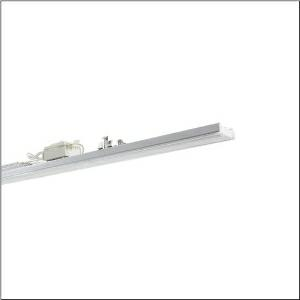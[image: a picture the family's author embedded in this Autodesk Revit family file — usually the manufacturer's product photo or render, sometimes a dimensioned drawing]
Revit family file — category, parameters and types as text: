
# Revit family: licross_11_recessed_mo_51tl12dv4fxg3c
name_source: partatom
category: Lighting Fixtures
units: mm (PartAtom-declared; Revit-internal decimal feet)

## family parameters
Cut with Voids When Loaded = No
Host = Face
Light Source = No
Part Type = Normal
Room Calculation Point = No
Round Connector Dimension = Use Diameter
Shared = No

## types (1)
- --- (1 x LED, 1010 lm, 5.5 W, 4000K)
    Apparent Load = 6 VA
    CIE Flux Codes = 67 92 99 100 100
    Color Rendering = 80
    Color Temperature = 4000K
    Default Elevation = 1800 mm
    Description = Licross 11 Recessed MO, luminaire insert, of sheet steel, coil coated, white, length: 2.250mm, width: 66mm, height: 67mm, LED rated luminous flux: 15.360lm, light colour: 840, SDCM (Standard Deviation of Colour Matching)MacAdam ≤ 2 SDCM (initial), control gear: DALI 2 (for two DALI lines), with plug, 6-pole, with phase selection, for trunking rail, 14-core, mains connection: 220..240V, AC, 50/60Hz, rated input power: 88W, for trunking rail, 14-core, internal wiring halogen-free, for emergency light function, converter,control gear: single battery element, battery: LiFePO4, 9Ah, primary optical cover: cover, of PMMA, light emission: direct distribution, primary light characteristic: symmetric, protection rating (complete): IP40, insulation class (complete): insulation class I (protective earthing), certification: CE, UKCA, protection symbol: D if used in an environment without relevant dust loads with corresponding accessories, impact resistance: IK06, permissible ambient temperature for indoor applications: +5..+35°C, standard: EN 60598-2-22, LABS conformity tested according to VDMA 24364:2018-05, reducing of maximum allowable ambient temperature of 5°C with ceiling mounting, corresponds to IFS (International Featured Standards) requirements for safety and quality in the food industry, The light source and the operating device comply with the requirements of the Ecodesign Regulation (EU) 2019/2020 and are replaceable in accordance with this regulation, packaging unit: 1 piece
    Height = 58 mm
    Lamp = 1 x LED
    Lamp Light Flux = 1010 lm
    Lamp Power = 5.5 W
    Lamp count = 1
    Length = 2250 mm
    Luminous efficacy = 184 lm/W
    Manufacturer = Siteco
    ModVariant = No
    Model = 51TL12DV4FXG3C
    Mounting Place = Ceiling
    Mounting Type = Pendant
    Number of Poles = 1
    OnlyDefault = Yes
    Power Factor = 1
    Product Name = Licross 11 Recessed MO
    Product group = luminaire insert | ceiling pendant
    ProductGroupID = 901
    Protection Class = Protection class I
    Protection Degree = IP 40
    RLX_Detail_Level = 1
    RLX_Emergency_Light_Flux = 0 lm
    RLX_Emergency_Type = 0
    RLX_Emergency_Type_DB = No
    RlxData = <blob elided: 30053 chars, md5=8b111d7f>
    Socket = socket
    Standby Power = 0 W
    System Light Flux = 1010 lm
    System Power = 6 W
    Type Comments = : emergency light operation: 3 h
    Type Image = l_1296930.jpg
    URL = http://relux.com
    VarID = @adj_090021
    Voltage = 0 V
    Weight = 0.00 kg
    Width = 66 mm

## geometry (parser evidence)
native form markers: Blend x4, Sweep x11
no freeform markers — native parametric forms only
